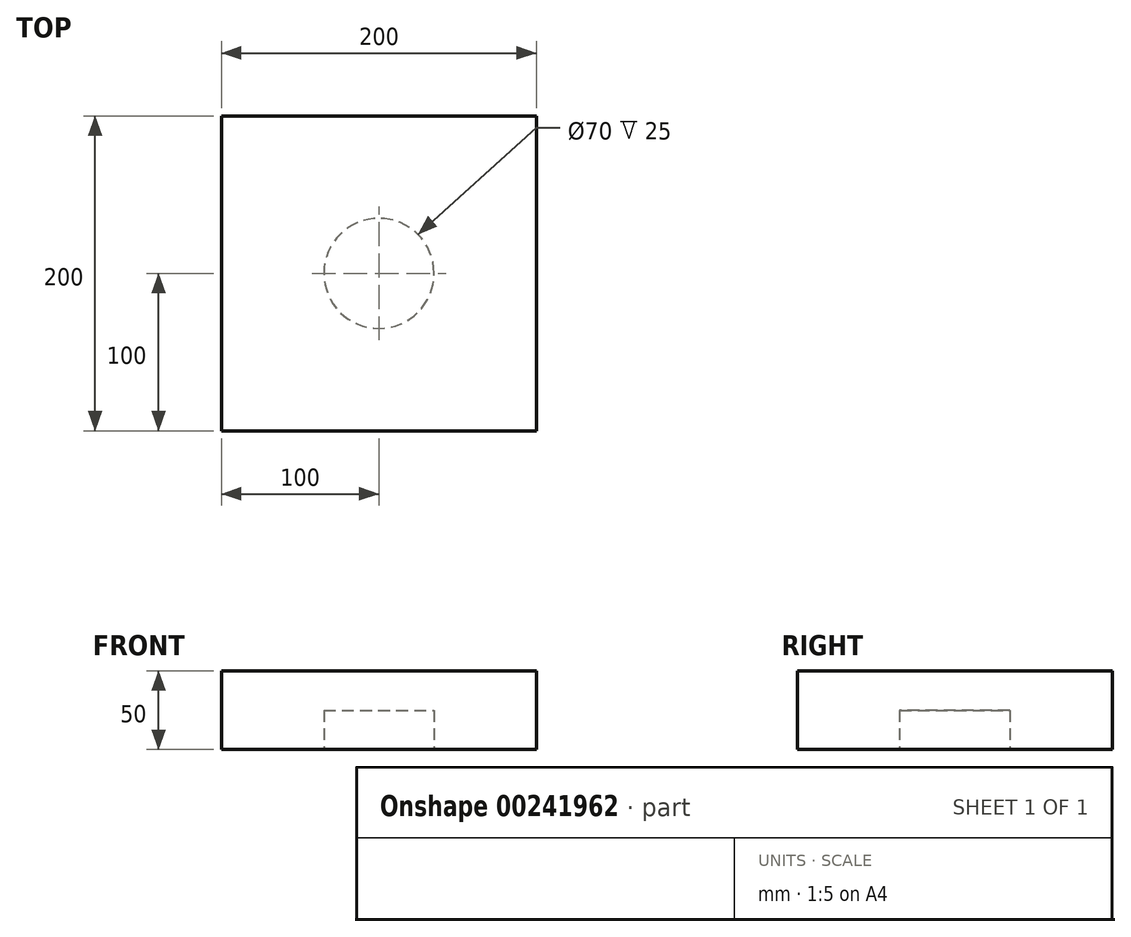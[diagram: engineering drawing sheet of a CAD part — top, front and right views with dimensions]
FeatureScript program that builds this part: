
annotation { "Feature Type Name" : "Feature", "Feature Type Description" : "" }
export const myFeature = defineFeature(function(context is Context, id is Id, definition is map)
    precondition{}
    {
        {
            var Q0;
            Q0=qCreatedBy(makeId("Top.planeOp"),FACE);
            var sketch = newSketch(context, id + "F0", { "sketchPlane" : qUnion([Q0])});
            skLineSegment(sketch, "E0.bottom", {"start": v(-100, 100) * mm, "end": v(100, 100) * mm});
            skLineSegment(sketch, "E0.top", {"start": v(-100, -100) * mm, "end": v(100, -100) * mm});
            skLineSegment(sketch, "E0.left", {"start": v(-100, 100) * mm, "end": v(-100, -100) * mm});
            skLineSegment(sketch, "E0.right", {"start": v(100, 100) * mm, "end": v(100, -100) * mm});
            skPoint(sketch, "E1", {"position": v(0, 100) * mm});
            skPoint(sketch, "E2", {"position": v(-100, 0) * mm});
            skSolve(sketch);
        }
        {
            var Q0;
            Q0 = qSketchRegion(id + "F0", true);
            extrude(context, id + "F1", {"entities" : qUnion([Q0]), "depth" : 50 * mm});
        }
        {
            var Q0;
            Q0=makeQuery(id+"F1.opExtrude","CAP_FACE",FACE,{"disambiguationData":[OSD([sQuery(id+"F0.wireOp",EDGE,"E0.bottom"),sQuery(id+"F0.wireOp",EDGE,"E0.top"),sQuery(id+"F0.wireOp",EDGE,"E0.left"),sQuery(id+"F0.wireOp",EDGE,"E0.right")])],"isStart":true});
            var sketch = newSketch(context, id + "F2", { "sketchPlane" : qUnion([Q0])});
            skCircle(sketch, "E3", {"center": v(0, 0) * mm, "radius": 35 * mm});
            skSolve(sketch);
        }
        {
            var Q0;
            Q0 = qSketchRegion(id + "F2", true);
            extrude(context, id + "F3", {"entities" : qUnion([Q0]), "operationType" : NewBodyOperationType.REMOVE, "oppositeDirection" : true, "depth" : 25 * mm});
        }
    });
